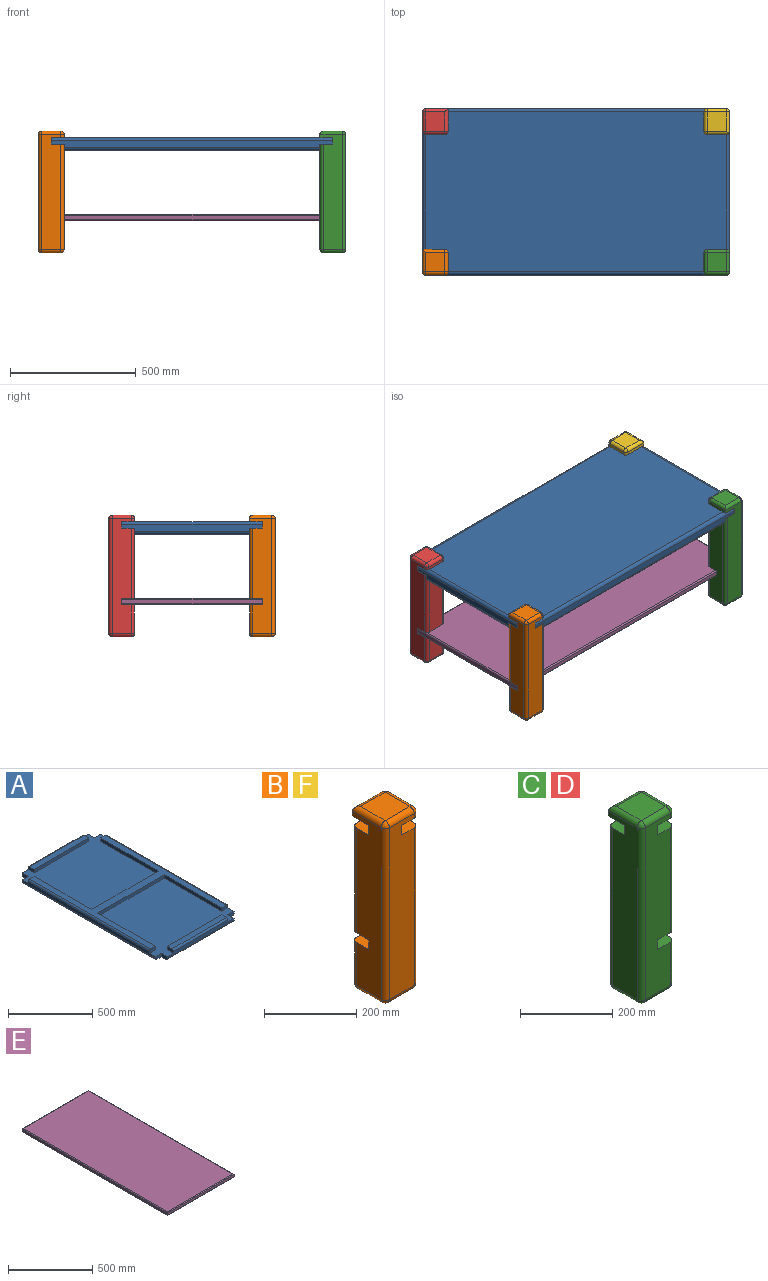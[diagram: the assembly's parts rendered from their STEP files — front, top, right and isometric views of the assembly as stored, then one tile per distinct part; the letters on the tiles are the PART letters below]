
ASSEMBLY  parts=6 mates=5
PART A: 42 faces, bbox 660.4x1219.2x50.8 mm
  f0: plane 1117.6x25.4mm, normal (-1,0,0), area 27096.7mm2, adj f1,f11,f16,f24,f26,f33,f37,f41
  f1: plane 50.8x25.4mm, normal (0,-1,0), area 1255.7mm2, adj f0,f2,f15,f33,f37
  f2: plane 50.8x25.4mm, normal (-1,0,0), area 1255.7mm2, adj f1,f3,f15,f33,f36
  f3: plane 558.8x25.4mm, normal (0,-1,0), area 12903.2mm2, adj f2,f4,f27,f29,f33,f36,f40
  f4: plane 50.8x25.4mm, normal (1,0,0), area 1255.7mm2, adj f3,f5,f15,f33,f36
  f5: plane 50.8x25.4mm, normal (0,-1,0), area 1255.7mm2, adj f4,f6,f15,f33,f35
  f6: plane 1117.6x25.4mm, normal (1,0,0), area 27096.7mm2, adj f5,f7,f20,f24,f30,f33,f35,f39
  f7: plane 50.8x25.4mm, normal (0,1,0), area 1255.7mm2, adj f6,f8,f15,f24,f35
  f8: plane 50.8x25.4mm, normal (1,0,0), area 1255.7mm2, adj f7,f9,f15,f24,f34
  f9: plane 558.8x25.4mm, normal (0,1,0), area 12903.2mm2, adj f8,f10,f21,f23,f24,f34,f38
  f10: plane 50.8x25.4mm, normal (-1,0,0), area 1255.7mm2, adj f9,f11,f15,f24,f34
  f11: plane 50.8x25.4mm, normal (0,1,0), area 1255.7mm2, adj f0,f10,f15,f24,f37
  f12: plane 457.2x38.1mm, normal (0,0,1), area 17419.3mm2, adj f27,f28,f29,f40
  f13: plane 1016x635mm, normal (0,0,1), area 105806.2mm2, adj f16,f17,f18,f19,f20,f25,f26,f30
  f14: plane 457.2x38.1mm, normal (0,0,1), area 17419.3mm2, adj f21,f22,f23,f38
  f15: plane 1193.8x635mm, normal (0,0,-1), area 752256.6mm2, adj f1,f2,f4,f5,f7,f8,f10,f11
  f16: plane 50.8x25.4mm, normal (0,1,0), area 1255.7mm2, adj f0,f13,f17,f24,f41
  f17: plane 482.6x25.4mm, normal (1,0,0), area 12258mm2, adj f13,f16,f18,f24
  f18: plane 558.8x25.4mm, normal (0,1,0), area 14193.5mm2, adj f13,f17,f19,f24
  f19: plane 482.6x25.4mm, normal (-1,0,0), area 12258mm2, adj f13,f18,f20,f24
  f20: plane 50.8x25.4mm, normal (0,1,0), area 1255.7mm2, adj f6,f13,f19,f24,f39
  f21: plane 50.8x25.4mm, normal (1,0,0), area 1255.7mm2, adj f9,f14,f22,f24,f38
  f22: plane 457.2x25.4mm, normal (0,-1,0), area 11612.9mm2, adj f14,f21,f23,f24
  f23: plane 50.8x25.4mm, normal (-1,0,0), area 1255.7mm2, adj f9,f14,f22,f24,f38
  f24: plane 660.4x584.2mm, normal (0,0,1), area 308386.5mm2, adj f0,f6,f7,f8,f9,f10,f11,f16
  f25: plane 482.6x25.4mm, normal (1,0,0), area 12258mm2, adj f13,f26,f32,f33
  f26: plane 50.8x25.4mm, normal (0,-1,0), area 1255.7mm2, adj f0,f13,f25,f33,f41
  f27: plane 50.8x25.4mm, normal (-1,0,0), area 1255.7mm2, adj f3,f12,f28,f33,f40
  f28: plane 457.2x25.4mm, normal (0,1,0), area 11612.9mm2, adj f12,f27,f29,f33
  f29: plane 50.8x25.4mm, normal (1,0,0), area 1255.7mm2, adj f3,f12,f28,f33,f40
  f30: plane 50.8x25.4mm, normal (0,-1,0), area 1255.7mm2, adj f6,f13,f31,f33,f39
  f31: plane 482.6x25.4mm, normal (-1,0,0), area 12258mm2, adj f13,f30,f32,f33
  f32: plane 558.8x25.4mm, normal (0,-1,0), area 14193.5mm2, adj f13,f25,f31,f33
  f33: plane 660.4x584.2mm, normal (0,0,1), area 308386.5mm2, adj f0,f1,f2,f3,f4,f5,f6,f25
  f34: cylinder r=12.7mm len=558.8mm, axis (-1,0,0), area 11147.6mm2, adj f8,f9,f10,f15
  f35: cylinder r=12.7mm len=1117.6mm, axis (0,1,0), area 22295.1mm2, adj f5,f6,f7,f15
  f36: cylinder r=12.7mm len=558.8mm, axis (1,0,0), area 11147.6mm2, adj f2,f3,f4,f15
  f37: cylinder r=12.7mm len=1117.6mm, axis (0,-1,0), area 22295.1mm2, adj f0,f1,f11,f15
  f38: cylinder r=12.7mm len=457.2mm, axis (1,0,0), area 9120.7mm2, adj f9,f14,f21,f23
  f39: cylinder r=12.7mm len=1016mm, axis (0,-1,0), area 20268.3mm2, adj f6,f13,f20,f30
  f40: cylinder r=12.7mm len=457.2mm, axis (-1,0,0), area 9120.7mm2, adj f3,f12,f27,f29
  f41: cylinder r=12.7mm len=1016mm, axis (0,1,0), area 20268.3mm2, adj f0,f13,f16,f26
PART B: 39 faces, bbox 101.6x101.6x482.6 mm
  f0: plane 114.3x76.2mm, normal (0,1,0), area 8709.7mm2, adj f29,f33,f35,f38
  f1: plane 457.2x88.9mm, normal (-1,0,0), area 33064.4mm2, adj f3,f8,f11,f13,f14,f21,f26,f32
  f2: cylinder r=12.7mm len=279.4mm, axis (0,0,1), area 5573.8mm2, adj f4,f7,f13,f36
  f3: cylinder r=12.7mm len=279.4mm, axis (0,0,-1), area 5573.8mm2, adj f1,f4,f13,f36
  f4: plane 279.4x76.2mm, normal (0,1,0), area 21290.3mm2, adj f2,f3,f13,f36
  f5: plane 76.2x12.7mm, normal (1,0,0), area 967.7mm2, adj f11,f15,f17,f18
  f6: plane 457.2x76.2mm, normal (0,-1,0), area 33870.9mm2, adj f11,f12,f13,f18,f22,f23,f26,f27
  f7: plane 419.1x76.2mm, normal (1,0,0), area 30967.7mm2, adj f2,f13,f23,f28,f29,f36,f37,f38
  f8: plane 88.9x12.7mm, normal (0,1,0), area 1129mm2, adj f1,f11,f15,f19
  f9: plane 76.2x76.2mm, normal (0,0,1), area 5806.4mm2, adj f17,f19,f21,f22
  f10: plane 76.2x76.2mm, normal (0,0,-1), area 5806.4mm2, adj f27,f28,f32,f33
  f11: plane 101.6x101.6mm, normal (0,0,-1), area 7672.7mm2, adj f1,f5,f6,f8,f12,f14,f15,f18
  f12: plane 50.8x25.4mm, normal (1,0,0), area 1290.3mm2, adj f6,f11,f13,f14
  f13: plane 101.6x101.6mm, normal (0,0,1), area 7638.1mm2, adj f1,f2,f3,f4,f6,f7,f12,f14
  f14: plane 50.8x25.4mm, normal (0,1,0), area 1290.3mm2, adj f1,f11,f12,f13
  f15: cylinder r=12.7mm len=12.7mm, axis (0,0,1), area 253.4mm2, adj f5,f8,f11,f16
  f16: sphere r=12.7mm, area 253.4mm2, adj f15,f17,f19
  f17: cylinder r=12.7mm len=76.2mm, axis (0,-1,0), area 1520.1mm2, adj f5,f9,f16,f20
  f18: cylinder r=12.7mm len=12.7mm, axis (0,0,-1), area 253.4mm2, adj f5,f6,f11,f20
  f19: cylinder r=12.7mm len=88.9mm, axis (1,0,0), area 1681.4mm2, adj f8,f9,f16,f21
  f20: sphere r=12.7mm, area 253.4mm2, adj f17,f18,f22
  f21: cylinder r=12.7mm len=88.9mm, axis (0,1,0), area 1681.4mm2, adj f1,f9,f19,f24
  f22: cylinder r=12.7mm len=76.2mm, axis (-1,0,0), area 1520.1mm2, adj f6,f9,f20,f24
  f23: cylinder r=12.7mm len=419.1mm, axis (0,0,-1), area 8360.7mm2, adj f6,f7,f13,f25
  f24: sphere r=12.7mm, area 253.4mm2, adj f21,f22,f26
  f25: sphere r=12.7mm, area 253.4mm2, adj f23,f27,f28
  f26: cylinder r=12.7mm len=457.2mm, axis (0,0,1), area 9120.7mm2, adj f1,f6,f24,f30
  f27: cylinder r=12.7mm len=76.2mm, axis (1,0,0), area 1520.1mm2, adj f6,f10,f25,f30
  f28: cylinder r=12.7mm len=76.2mm, axis (0,1,0), area 1520.1mm2, adj f7,f10,f25,f31
  f29: cylinder r=12.7mm len=114.3mm, axis (0,0,1), area 2280.2mm2, adj f0,f7,f31,f38
  f30: sphere r=12.7mm, area 253.4mm2, adj f26,f27,f32
  f31: sphere r=12.7mm, area 253.4mm2, adj f28,f29,f33
  f32: cylinder r=12.7mm len=76.2mm, axis (0,-1,0), area 1520.1mm2, adj f1,f10,f30,f34
  f33: cylinder r=12.7mm len=76.2mm, axis (-1,0,0), area 1520.1mm2, adj f0,f10,f31,f34
  f34: sphere r=12.7mm, area 253.4mm2, adj f32,f33,f35
  f35: cylinder r=12.7mm len=114.3mm, axis (0,0,-1), area 2280.2mm2, adj f0,f1,f34,f38
  f36: plane 101.6x50.8mm, normal (0,0,-1), area 5092.1mm2, adj f1,f2,f3,f4,f7,f37
  f37: plane 101.6x25.4mm, normal (0,1,0), area 2580.6mm2, adj f1,f7,f36,f38
  f38: plane 101.6x50.8mm, normal (0,0,1), area 5092.1mm2, adj f0,f1,f7,f29,f35,f37
PART C: 39 faces, bbox 101.6x101.6x482.6 mm
  f0: plane 419.1x76.2mm, normal (0,1,0), area 30967.7mm2, adj f9,f10,f11,f14,f30,f34,f36,f38
  f1: plane 457.2x88.9mm, normal (-1,0,0), area 34032.2mm2, adj f5,f12,f14,f15,f22,f27,f33,f36
  f2: plane 76.2x12.7mm, normal (1,0,0), area 967.7mm2, adj f12,f16,f18,f19
  f3: plane 279.4x76.2mm, normal (1,0,0), area 21290.3mm2, adj f10,f14,f37,f38
  f4: plane 457.2x76.2mm, normal (0,-1,0), area 32903.2mm2, adj f9,f10,f11,f12,f13,f14,f19,f23
  f5: plane 88.9x12.7mm, normal (0,1,0), area 1129mm2, adj f1,f12,f16,f20
  f6: plane 114.3x76.2mm, normal (1,0,0), area 8709.7mm2, adj f9,f24,f29,f30
  f7: plane 76.2x76.2mm, normal (0,0,1), area 5806.4mm2, adj f18,f20,f22,f23
  f8: plane 76.2x76.2mm, normal (0,0,-1), area 5806.4mm2, adj f28,f29,f33,f34
  f9: plane 101.6x50.8mm, normal (0,0,1), area 5092.1mm2, adj f0,f4,f6,f11,f24,f30
  f10: plane 101.6x50.8mm, normal (0,0,-1), area 5092.1mm2, adj f0,f3,f4,f11,f37,f38
  f11: plane 101.6x25.4mm, normal (1,0,0), area 2580.6mm2, adj f0,f4,f9,f10
  f12: plane 101.6x101.6mm, normal (0,0,-1), area 7672.7mm2, adj f1,f2,f4,f5,f13,f15,f16,f19
  f13: plane 50.8x25.4mm, normal (1,0,0), area 1290.3mm2, adj f4,f12,f14,f15
  f14: plane 101.6x101.6mm, normal (0,0,1), area 7638.1mm2, adj f0,f1,f3,f4,f13,f15,f36,f37
  f15: plane 50.8x25.4mm, normal (0,1,0), area 1290.3mm2, adj f1,f12,f13,f14
  f16: cylinder r=12.7mm len=12.7mm, axis (0,0,1), area 253.4mm2, adj f2,f5,f12,f17
  f17: sphere r=12.7mm, area 253.4mm2, adj f16,f18,f20
  f18: cylinder r=12.7mm len=76.2mm, axis (0,-1,0), area 1520.1mm2, adj f2,f7,f17,f21
  f19: cylinder r=12.7mm len=12.7mm, axis (0,0,-1), area 253.4mm2, adj f2,f4,f12,f21
  f20: cylinder r=12.7mm len=88.9mm, axis (1,0,0), area 1681.4mm2, adj f5,f7,f17,f22
  f21: sphere r=12.7mm, area 253.4mm2, adj f18,f19,f23
  f22: cylinder r=12.7mm len=88.9mm, axis (0,1,0), area 1681.4mm2, adj f1,f7,f20,f25
  f23: cylinder r=12.7mm len=76.2mm, axis (-1,0,0), area 1520.1mm2, adj f4,f7,f21,f25
  f24: cylinder r=12.7mm len=114.3mm, axis (0,0,-1), area 2280.2mm2, adj f4,f6,f9,f26
  f25: sphere r=12.7mm, area 253.4mm2, adj f22,f23,f27
  f26: sphere r=12.7mm, area 253.4mm2, adj f24,f28,f29
  f27: cylinder r=12.7mm len=457.2mm, axis (0,0,1), area 9120.7mm2, adj f1,f4,f25,f31
  f28: cylinder r=12.7mm len=76.2mm, axis (1,0,0), area 1520.1mm2, adj f4,f8,f26,f31
  f29: cylinder r=12.7mm len=76.2mm, axis (0,1,0), area 1520.1mm2, adj f6,f8,f26,f32
  f30: cylinder r=12.7mm len=114.3mm, axis (0,0,1), area 2280.2mm2, adj f0,f6,f9,f32
  f31: sphere r=12.7mm, area 253.4mm2, adj f27,f28,f33
  f32: sphere r=12.7mm, area 253.4mm2, adj f29,f30,f34
  f33: cylinder r=12.7mm len=76.2mm, axis (0,-1,0), area 1520.1mm2, adj f1,f8,f31,f35
  f34: cylinder r=12.7mm len=76.2mm, axis (-1,0,0), area 1520.1mm2, adj f0,f8,f32,f35
  f35: sphere r=12.7mm, area 253.4mm2, adj f33,f34,f36
  f36: cylinder r=12.7mm len=419.1mm, axis (0,0,-1), area 8360.7mm2, adj f0,f1,f14,f35
  f37: cylinder r=12.7mm len=279.4mm, axis (0,0,-1), area 5573.8mm2, adj f3,f4,f10,f14
  f38: cylinder r=12.7mm len=279.4mm, axis (0,0,1), area 5573.8mm2, adj f0,f3,f10,f14
PART D: same geometry as C
PART E: 14 faces, bbox 558.8x1219.2x25.4 mm
  f0: plane 1219.2x15.24mm, normal (-1,0,0), area 18580.6mm2, adj f1,f3,f6,f10
  f1: plane 558.8x15.24mm, normal (0,-1,0), area 8516.1mm2, adj f0,f2,f7,f11
  f2: plane 1219.2x15.24mm, normal (1,0,0), area 18580.6mm2, adj f1,f3,f9,f13
  f3: plane 558.8x15.24mm, normal (0,1,0), area 8516.1mm2, adj f0,f2,f8,f12
  f4: plane 1209.04x548.64mm, normal (0,0,1), area 663327.7mm2, adj f10,f11,f12,f13
  f5: plane 1209.04x548.64mm, normal (0,0,-1), area 663327.7mm2, adj f6,f7,f8,f9
  f6: cylinder r=5.08mm len=1219.2mm, axis (0,-1,0), area 9699.3mm2, adj f0,f5,f7,f8
  f7: cylinder r=5.08mm len=558.8mm, axis (1,0,0), area 4429.6mm2, adj f1,f5,f6,f9
  f8: cylinder r=5.08mm len=558.8mm, axis (-1,0,0), area 4429.6mm2, adj f3,f5,f6,f9
  f9: cylinder r=5.08mm len=1219.2mm, axis (0,1,0), area 9699.3mm2, adj f2,f5,f7,f8
  f10: cylinder r=5.08mm len=1219.2mm, axis (0,1,0), area 9699.3mm2, adj f0,f4,f11,f12
  f11: cylinder r=5.08mm len=558.8mm, axis (-1,0,0), area 4429.6mm2, adj f1,f4,f10,f13
  f12: cylinder r=5.08mm len=558.8mm, axis (1,0,0), area 4429.6mm2, adj f3,f4,f10,f13
  f13: cylinder r=5.08mm len=1219.2mm, axis (0,-1,0), area 9699.3mm2, adj f2,f4,f11,f12
PART F: same geometry as B
PLACE A rot(axis=(0.71,-0.71,0),180deg) t=(63.57,108.21,-75.32)mm
PLACE B t=(-1104.83,-552.19,-532.52)mm
PLACE C rot(axis=(0,0,1),90deg) t=(114.37,-552.19,-532.52)mm
PLACE D rot(axis=(0,0,-1),90deg) t=(-1104.83,108.21,-532.52)mm
PLACE E rot(axis=(0,0,1),90deg) t=(114.37,-501.39,-405.52)mm
PLACE F rot(axis=(0,0,1),180deg) t=(114.37,108.21,-532.52)mm
MATE fastened F.f1 <-> A.f3  axis (1,0,0) through (114.37,57.41,-100.72)mm
MATE fastened E.f3 <-> B.f1  axis (-1,0,0) through (-1104.83,-501.39,-392.82)mm
MATE fastened A.f3 <-> C.f4  axis (1,0,0) through (114.37,-501.39,-100.72)mm
MATE fastened B.f1 <-> A.f9  axis (-1,0,0) through (-1104.83,-501.39,-100.72)mm
MATE fastened D.f4 <-> A.f9  axis (-1,0,0) through (-1104.83,57.41,-100.72)mm
